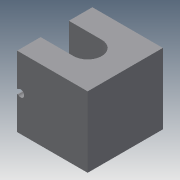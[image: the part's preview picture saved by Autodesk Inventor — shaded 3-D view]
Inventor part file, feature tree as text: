
AUTODESK INVENTOR PART (.ipt)
format: ipt  version: 2013 (Build 170138000, 138)  size: 233,984 bytes
history: native  units: mm
features: sketch x24, extrude x18, hole x4, fillet x1
ambient origin geometry x8: Origin, YZ Plane, XZ Plane, XY Plane, X Axis, Y Axis, Z Axis, Center Point
bodies: Solid1 (feature_tree)
feature tree (47):
  extrude  "Extrusion1"  Depth=20.0mm
  extrude  "Extrusion2"  Depth=3.0mm
  extrude  "Extrusion3"  Depth=1.0mm
  extrude  "Extrusion4"  Depth=10.0mm TaperAngle=0.0deg
  extrude  "Extrusion5"  Depth=10.0mm TaperAngle=0.0deg
  extrude  "Extrusion6"  Depth=12.0mm TaperAngle=0.0deg
  extrude  "Extrusion7"  Depth=30.0mm TaperAngle=0.0deg
  extrude  "Extrusion8"  Depth=2.0mm
  fillet  "Fillet1"  Radius=10.0mm
  extrude  "Extrusion9"  Depth=5.0mm TaperAngle=0.0deg
  extrude  "Extrusion10"  Depth=3.0mm
  sketch  "Sketch11"  dims[d32=3.0mm d33=3.0mm]
  sketch  "Sketch12"  dims[d34=3.0mm d35=5.0mm d36=0.0mm]
  sketch  "Sketch13"  dims[d37=5.0mm d38=0.0mm d39=5.0mm d40=0.0mm]
  sketch  "Sketch14"  dims[d41=5.0mm d42=0.0mm d43=5.0mm d44=0.0mm]
  sketch  "Sketch15"  dims[d45=5.0mm d46=0.0mm d47=5.0mm d48=0.0mm]
  extrude  "Extrusion11"  Depth=3.0mm
  extrude  "Extrusion12"  Depth=5.0mm TaperAngle=0.0deg
  extrude  "Extrusion13"  Depth=5.0mm TaperAngle=0.0deg
  extrude  "Extrusion14"  Depth=5.0mm TaperAngle=0.0deg
  sketch  "Sketch16"  dims[d49=5.0mm d50=0.0mm d51=4.0mm]
  sketch  "Sketch17"  dims[d52=3.0mm d53=4.0mm]
  sketch  "Sketch18"  dims[d54=3.0mm d55=4.0mm]
  sketch  "Sketch19"  dims[d56=3.0mm d57=4.0mm]
  sketch  "Sketch20"  dims[d58=3.0mm d59=2.459mm d60=3.0mm]
  extrude  "Extrusion15"  Depth=5.0mm TaperAngle=0.0deg
  extrude  "Extrusion16"  Depth=4.0mm
  extrude  "Extrusion17"  Depth=4.0mm
  extrude  "Extrusion18"  Depth=4.0mm
  sketch  "Sketch21"  dims[d61=4.0mm d62=2.0mm d63=90.0deg d64=8.0mm d65=20.594885mm d66=2.459mm d67=3.0mm]
  sketch  "Sketch22"  dims[d68=4.0mm d69=2.0mm d70=90.0deg d71=8.0mm d72=20.594885mm d73=2.459mm d74=3.0mm]
  sketch  "Sketch23"  dims[d75=4.0mm d76=2.0mm d77=90.0deg d78=8.0mm d79=20.594885mm]
  sketch  "Sketch24"  dims[d80=2.459mm d81=3.0mm d82=4.0mm d83=2.0mm d84=90.0deg d85=8.0mm d86=20.594885mm]
  hole  "Hole1"  [1 undecoded]
  hole  "Hole2"  [1 undecoded]
  hole  "Hole3"  [1 undecoded]
  hole  "Hole4"  [1 undecoded]
  sketch  "Sketch1"  dims[d0=30.0mm d1=20.0mm]
  sketch  "Sketch2"  dims[d2=10.0mm d3=0.0mm d4=3.0mm]
  sketch  "Sketch3"  dims[d5=10.0mm d6=0.0mm d7=1.0mm]
  sketch  "Sketch4"  dims[d8=1.0mm d9=10.0mm d10=0.0mm]
  sketch  "Sketch5"  dims[d11=2.0mm d12=10.0mm d13=0.0mm]
  sketch  "Sketch6"  dims[d14=10.0mm d15=12.0mm d16=0.0mm]
  sketch  "Sketch7"  dims[d17=10.0mm d18=30.0mm d19=0.0mm]
  sketch  "Sketch8"  dims[d21=10.0mm d22=0.0mm d23=2.0mm d24=10.0mm d25=0.0mm]
  sketch  "Sketch9"  dims[d26=6.0mm d27=5.0mm d28=0.0mm]
  sketch  "Sketch10"  dims[d29=5.0mm d30=0.0mm d31=3.0mm]
note: 4 required parameter values undecoded (feature->parameter linkage not recoverable at this tier; creation-order binding heuristic only, values carry confidence <= 0.55)
